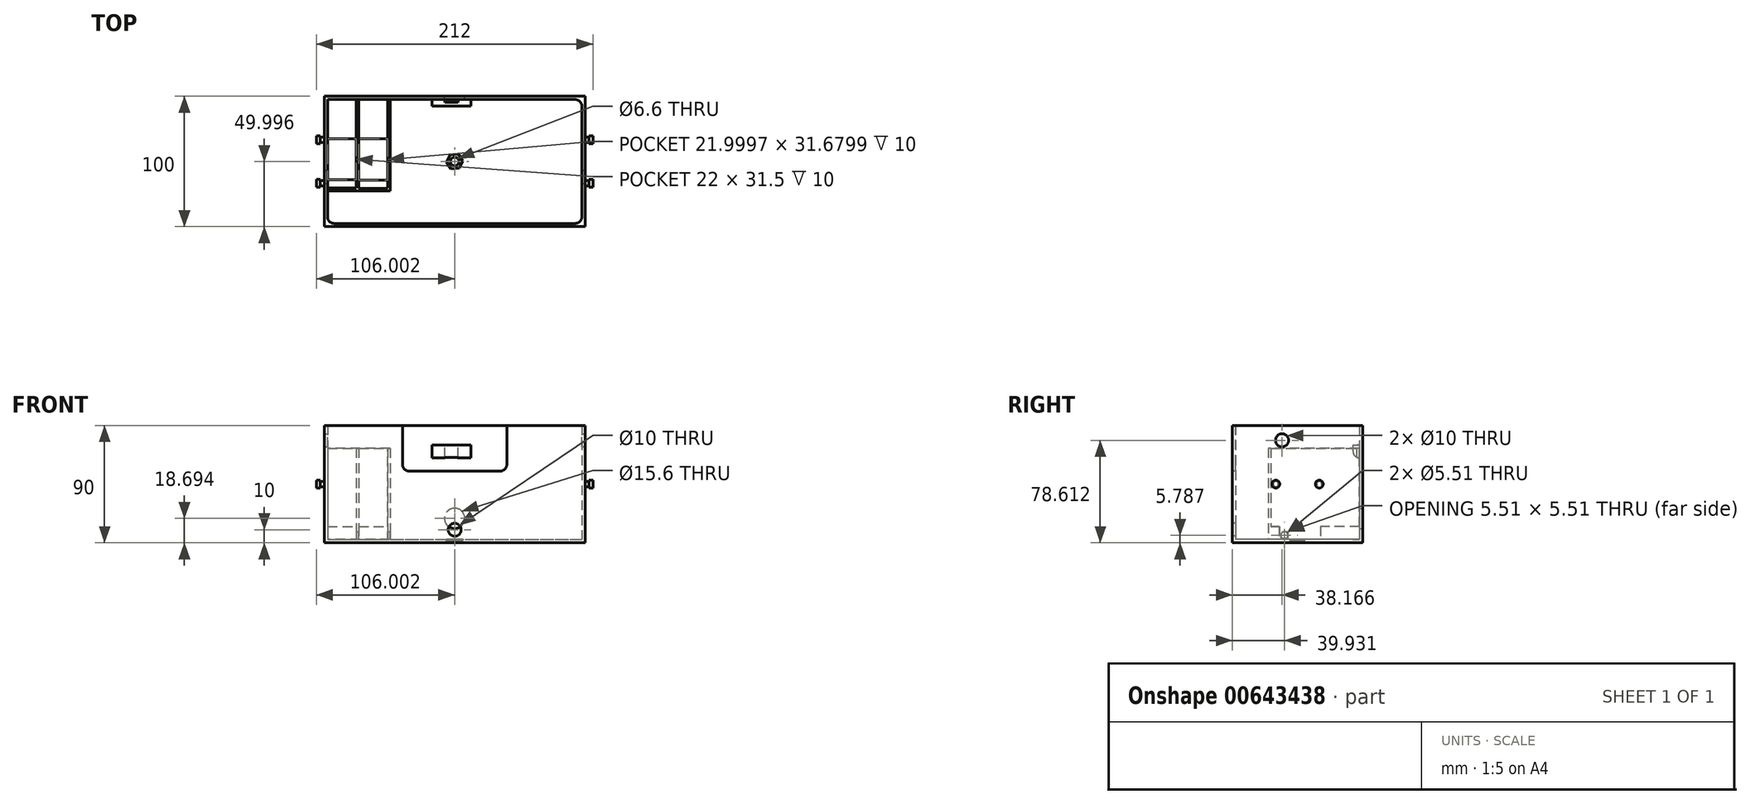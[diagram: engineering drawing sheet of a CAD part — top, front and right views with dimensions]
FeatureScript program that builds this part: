
annotation { "Feature Type Name" : "Feature", "Feature Type Description" : "" }
export const myFeature = defineFeature(function(context is Context, id is Id, definition is map)
    precondition{}
    {
        {
            var Q0;
            Q0=qCreatedBy(makeId("Top.planeOp"),FACE);
            var sketch = newSketch(context, id + "F0", { "sketchPlane" : qUnion([Q0])});
            skLineSegment(sketch, "E0.bottom", {"start": v(-106.92, 32.06) * mm, "end": v(93.08, 32.06) * mm});
            skLineSegment(sketch, "E0.top", {"start": v(-106.92, -67.94) * mm, "end": v(93.08, -67.94) * mm});
            skLineSegment(sketch, "E0.left", {"start": v(-106.92, 32.06) * mm, "end": v(-106.92, -67.94) * mm});
            skLineSegment(sketch, "E0.right", {"start": v(93.08, 32.06) * mm, "end": v(93.08, -67.94) * mm});
            skSolve(sketch);
        }
        {
            var Q0;
            Q0=makeQuery(id+"F0.imprint","IMPRINT",FACE,{"disambiguationData":[TD([[makeQuery(id+"F0.imprint","IMPRINT",EDGE,{"derivedFrom":sQuery(id+"F0.wireOp",EDGE,"E0.bottom")}),-1.0]])]});
            var Q1;
            Q1 = qSketchRegion(id + "FvAQ6DcHnj1znLy_1", true);
            extrude(context, id + "F1", {"entities" : qUnion([Q0, Q1]), "depth" : 90 * mm, "offsetDistance" : 25 * mm});
        }
        {
            var Q0;
            Q0=makeQuery(id+"F1.opExtrude","CAP_FACE",FACE,{"disambiguationData":[OSD([sQuery(id+"F0.wireOp",EDGE,"E0.bottom"),sQuery(id+"F0.wireOp",EDGE,"E0.top"),sQuery(id+"F0.wireOp",EDGE,"E0.left"),sQuery(id+"F0.wireOp",EDGE,"E0.right")])],"isStart":false});
            shell(context, id + "F2", {"entities" : qUnion([Q0]), "thickness" : 2.5 * mm});
        }
        {
            var Q0;
            Q0=makeQuery(id+"F2.opShell","OFFSET_FACE",FACE,{"disambiguationData":[OSD([sQuery(id+"F0.wireOp",EDGE,"E0.bottom"),sQuery(id+"F0.wireOp",EDGE,"E0.top"),sQuery(id+"F0.wireOp",EDGE,"E0.left"),sQuery(id+"F0.wireOp",EDGE,"E0.right")])]});
            var sketch = newSketch(context, id + "F3", { "sketchPlane" : qUnion([Q0])});
            skLineSegment(sketch, "E1", {"start": v(-104.42, 29.56) * mm, "end": v(-104.42, -38.44) * mm});
            skLineSegment(sketch, "E2", {"start": v(-104.42, -38.44) * mm, "end": v(-82.42, -38.44) * mm});
            skLineSegment(sketch, "E3", {"start": v(-82.42, -38.44) * mm, "end": v(-82.42, 29.56) * mm});
            skLineSegment(sketch, "E4", {"start": v(-82.42, 29.56) * mm, "end": v(-104.42, 29.56) * mm});
            skLineSegment(sketch, "E5", {"start": v(-82.42, 29.56) * mm, "end": v(-80.42, 29.56) * mm});
            skLineSegment(sketch, "E6", {"start": v(-80.42, 29.56) * mm, "end": v(-80.42, -38.62) * mm});
            skLineSegment(sketch, "E7", {"start": v(-80.42, -38.62) * mm, "end": v(-80.42, -40.44) * mm});
            skLineSegment(sketch, "E8", {"start": v(-80.42, -40.44) * mm, "end": v(-82.42, -40.44) * mm});
            skLineSegment(sketch, "E9", {"start": v(-82.42, -40.44) * mm, "end": v(-104.42, -40.44) * mm});
            skLineSegment(sketch, "E10", {"start": v(-104.42, -40.44) * mm, "end": v(-104.42, -38.44) * mm});
            skLineSegment(sketch, "E11", {"start": v(-80.42, 29.56) * mm, "end": v(-58.42, 29.56) * mm});
            skLineSegment(sketch, "E12", {"start": v(-58.42, 29.56) * mm, "end": v(-56.42, 29.56) * mm});
            skLineSegment(sketch, "E13", {"start": v(-56.42, 29.56) * mm, "end": v(-56.42, -38.44) * mm});
            skLineSegment(sketch, "E14", {"start": v(-56.42, -38.44) * mm, "end": v(-56.42, -40.44) * mm});
            skLineSegment(sketch, "E15", {"start": v(-56.42, -40.44) * mm, "end": v(-80.42, -40.44) * mm});
            skLineSegment(sketch, "E16", {"start": v(-80.42, -38.62) * mm, "end": v(-58.42, -38.44) * mm});
            skLineSegment(sketch, "E17", {"start": v(-58.42, -38.44) * mm, "end": v(-58.42, 29.56) * mm});
            skSolve(sketch);
        }
        {
            var Q0;
            Q0=makeQuery(id+"F3.imprint","IMPRINT",FACE,{"disambiguationData":[TD([[makeQuery(id+"F3.imprint","IMPRINT",EDGE,{"derivedFrom":sQuery(id+"F3.wireOp",EDGE,"E2")}),-1.0]])]});
            var Q1;
            Q1=makeQuery(id+"F3.imprint","IMPRINT",FACE,{"disambiguationData":[TD([[makeQuery(id+"F3.imprint","IMPRINT",EDGE,{"derivedFrom":sQuery(id+"F3.wireOp",EDGE,"E7")}),1.0]])]});
            extrude(context, id + "F4", {"entities" : qUnion([Q0, Q1]), "operationType" : NewBodyOperationType.ADD, "depth" : 70 * mm, "offsetDistance" : 25 * mm});
        }
        {
            var Q0;
            Q0=makeQuery(id+"F1.opExtrude","SWEPT_FACE",FACE,{"disambiguationData":[OSD([sQuery(id+"F0.wireOp",EDGE,"E0.top")])]});
            var sketch = newSketch(context, id + "F5", { "sketchPlane" : qUnion([Q0])});
            skLineSegment(sketch, "E18", {"start": v(-106.92, 90) * mm, "end": v(-46.92, 90) * mm, "construction": true});
            skLineSegment(sketch, "E19", {"start": v(-46.92, 90) * mm, "end": v(-46.92, 55) * mm});
            skLineSegment(sketch, "E20", {"start": v(-46.92, 55) * mm, "end": v(33.08, 55) * mm});
            skLineSegment(sketch, "E21", {"start": v(33.08, 55) * mm, "end": v(33.08, 90) * mm});
            skLineSegment(sketch, "E22", {"start": v(33.08, 90) * mm, "end": v(93.08, 90) * mm, "construction": true});
            skLineSegment(sketch, "E23", {"start": v(-6.92, 55) * mm, "end": v(-6.92, 10) * mm, "construction": true});
            skCircle(sketch, "E24", {"center": v(-6.92, 10) * mm, "radius": 5 * mm});
            skSolve(sketch);
        }
        {
            var Q0;
            {var subQ0=sQuery(id+"F5.wireOp",EDGE,"E19");Q0=makeQuery(id+"F5.imprint","IMPRINT",FACE,{"disambiguationData":[TD([[makeQuery(id+"F5.imprint","IMPRINT",EDGE,{"derivedFrom":subQ0}),1.0]])]});}
            var Q1;
            Q1=makeQuery(id+"F5.imprint","IMPRINT",FACE,{"disambiguationData":[TD([[makeQuery(id+"F5.imprint","IMPRINT",EDGE,{"derivedFrom":sQuery(id+"F5.wireOp",EDGE,"E24")}),1.0]])]});
            extrude(context, id + "F6", {"entities" : qUnion([Q0, Q1]), "operationType" : NewBodyOperationType.REMOVE, "oppositeDirection" : true, "depth" : 3 * mm, "offsetDistance" : 25 * mm});
        }
        {
            var Q0;
            Q0=makeQuery(id+"F1.opExtrude","CAP_FACE",FACE,{"disambiguationData":[OSD([sQuery(id+"F0.wireOp",EDGE,"E0.bottom"),sQuery(id+"F0.wireOp",EDGE,"E0.top"),sQuery(id+"F0.wireOp",EDGE,"E0.left"),sQuery(id+"F0.wireOp",EDGE,"E0.right")])],"isStart":true});
            var sketch = newSketch(context, id + "F7", { "sketchPlane" : qUnion([Q0])});
            skLineSegment(sketch, "E25", {"start": v(-6.92, 67.94) * mm, "end": v(-6.92, -32.06) * mm});
            skLineSegment(sketch, "E26", {"start": v(-106.92, 17.94) * mm, "end": v(93.08, 17.94) * mm, "construction": true});
            skCircle(sketch, "E27", {"center": v(-6.92, 17.94) * mm, "radius": 5.55 * mm, "construction": true});
            skLineSegment(sketch, "E28", {"start": v(-12.47, 14.74) * mm, "end": v(-12.47, 21.15) * mm});
            skLineSegment(sketch, "E29", {"start": v(-12.47, 21.15) * mm, "end": v(-6.92, 24.35) * mm});
            skLineSegment(sketch, "E30", {"start": v(-6.92, 24.35) * mm, "end": v(-1.37, 21.15) * mm});
            skLineSegment(sketch, "E31", {"start": v(-1.37, 21.15) * mm, "end": v(-1.37, 14.74) * mm});
            skLineSegment(sketch, "E32", {"start": v(-1.37, 14.74) * mm, "end": v(-6.92, 11.54) * mm});
            skLineSegment(sketch, "E33", {"start": v(-6.92, 11.54) * mm, "end": v(-12.47, 14.74) * mm});
            skCircle(sketch, "E34", {"center": v(-6.92, 17.94) * mm, "radius": 3.3 * mm});
            skSolve(sketch);
        }
        {
            var Q0;
            {var subQ0=sQuery(id+"F7.wireOp",EDGE,"E34");var subQ1=sQuery(id+"F7.wireOp",EDGE,"E25");var subQ2=makeQuery(id+"F7.imprint","INTERSECT",VERTEX,{"disambiguationData":[OD(0.0)],"derivedFrom":[subQ1,subQ0]});Q0=makeQuery(id+"F7.imprint","IMPRINT",FACE,{"disambiguationData":[TD([[makeQuery(id+"F7.imprint","IMPRINT",EDGE,{"disambiguationData":[TD([[subQ2,-1.0]])],"derivedFrom":subQ1}),1.0]])]});}
            var Q1;
            {var subQ0=sQuery(id+"F7.wireOp",EDGE,"E34");var subQ1=sQuery(id+"F7.wireOp",EDGE,"E25");var subQ2=makeQuery(id+"F7.imprint","INTERSECT",VERTEX,{"disambiguationData":[OD(0.0)],"derivedFrom":[subQ1,subQ0]});Q1=makeQuery(id+"F7.imprint","IMPRINT",FACE,{"disambiguationData":[TD([[makeQuery(id+"F7.imprint","IMPRINT",EDGE,{"disambiguationData":[TD([[subQ2,-1.0]])],"derivedFrom":subQ1}),-1.0]])]});}
            extrude(context, id + "F8", {"entities" : qUnion([Q0, Q1]), "operationType" : NewBodyOperationType.REMOVE, "oppositeDirection" : true, "depth" : 3 * mm, "offsetDistance" : 25 * mm});
        }
        {
            var Q0;
            {var subQ0=sQuery(id+"F0.wireOp",EDGE,"E0.right");var subQ1=sQuery(id+"F0.wireOp",EDGE,"E0.left");var subQ2=sQuery(id+"F0.wireOp",EDGE,"E0.top");var subQ3=sQuery(id+"F0.wireOp",EDGE,"E0.bottom");Q0=makeQuery(id+"F4.boolean.opBoolean","SPLIT",FACE,{"disambiguationData":[TD([makeQuery(id+"F2.opShell","OFFSET_FACE",FACE,{"disambiguationData":[OSD([subQ2])]})])],"derivedFrom":makeQuery(id+"F2.opShell","OFFSET_FACE",FACE,{"disambiguationData":[OSD([subQ3,subQ2,subQ1,subQ0])]})});}
            var sketch = newSketch(context, id + "F9", { "sketchPlane" : qUnion([Q0])});
            skCircle(sketch, "E35.cCircle", {"center": v(-6.92, -17.94) * mm, "radius": 6.25 * mm, "construction": true});
            skLineSegment(sketch, "E35.0", {"start": v(-10.37, -12.74) * mm, "end": v(-4.13, -12.35) * mm});
            skLineSegment(sketch, "E35.1", {"start": v(-4.13, -12.35) * mm, "end": v(-0.68, -17.56) * mm});
            skLineSegment(sketch, "E35.2", {"start": v(-0.68, -17.56) * mm, "end": v(-3.46, -23.15) * mm});
            skLineSegment(sketch, "E35.3", {"start": v(-3.46, -23.15) * mm, "end": v(-9.7, -23.54) * mm});
            skLineSegment(sketch, "E35.4", {"start": v(-9.7, -23.54) * mm, "end": v(-13.16, -18.33) * mm});
            skLineSegment(sketch, "E35.5", {"start": v(-13.16, -18.33) * mm, "end": v(-10.37, -12.74) * mm});
            skSolve(sketch);
        }
        {
            var Q0;
            Q0=makeQuery(id+"F9.imprint","IMPRINT",FACE,{"disambiguationData":[TD([[makeQuery(id+"F9.imprint","IMPRINT",EDGE,{"derivedFrom":sQuery(id+"F9.wireOp",EDGE,"E35.0")}),-1.0]])]});
            extrude(context, id + "F10", {"entities" : qUnion([Q0]), "operationType" : NewBodyOperationType.REMOVE, "oppositeDirection" : true, "depth" : 1.5 * mm, "offsetDistance" : 25 * mm});
        }
        {
            var Q0;
            Q0=makeQuery(id+"F1.opExtrude","SWEPT_FACE",FACE,{"disambiguationData":[OSD([sQuery(id+"F0.wireOp",EDGE,"E0.bottom")])]});
            var sketch = newSketch(context, id + "F11", { "sketchPlane" : qUnion([Q0])});
            skCircle(sketch, "E36", {"center": v(6.92, 18.7) * mm, "radius": 7.8 * mm});
            skPoint(sketch, "E36.centerSnap0", {"position": v(6.92, 0) * mm});
            skSolve(sketch);
        }
        {
            var Q0;
            Q0=makeQuery(id+"F11.imprint","IMPRINT",FACE,{"disambiguationData":[TD([[makeQuery(id+"F11.imprint","IMPRINT",EDGE,{"derivedFrom":sQuery(id+"F11.wireOp",EDGE,"E36")}),1.0]])]});
            extrude(context, id + "F12", {"entities" : qUnion([Q0]), "operationType" : NewBodyOperationType.REMOVE, "oppositeDirection" : true, "depth" : 3 * mm, "offsetDistance" : 25 * mm});
        }
        {
            var Q0;
            Q0=makeQuery(id+"F2.opShell","OFFSET_EDGE",EDGE,{"disambiguationData":[OSD([sQuery(id+"F0.wireOp",EDGE,"E0.bottom"),sQuery(id+"F0.wireOp",EDGE,"E0.right")])]});
            var Q1;
            Q1=makeQuery(id+"F2.opShell","OFFSET_EDGE",EDGE,{"disambiguationData":[OSD([sQuery(id+"F0.wireOp",EDGE,"E0.top"),sQuery(id+"F0.wireOp",EDGE,"E0.right")])]});
            var Q2;
            Q2=makeQuery(id+"F2.opShell","OFFSET_EDGE",EDGE,{"disambiguationData":[OSD([sQuery(id+"F0.wireOp",EDGE,"E0.top"),sQuery(id+"F0.wireOp",EDGE,"E0.left")])]});
            fillet(context, id + "F13", {"entities" : qUnion([Q0, Q1, Q2]), "radius" : 5 * mm, "tangentPropagation" : true, "allowEdgeOverflow" : false});
        }
        {
            var Q0;
            Q0=makeQuery(id+"F6.boolean.opBoolean","COPY",EDGE,{"derivedFrom":makeQuery(id+"F6.opExtrude","SWEPT_EDGE",EDGE,{"disambiguationData":[OSD([sQuery(id+"F5.wireOp",EDGE,"E20"),sQuery(id+"F5.wireOp",EDGE,"E21")])]})});
            var Q1;
            Q1=makeQuery(id+"F6.boolean.opBoolean","COPY",EDGE,{"derivedFrom":makeQuery(id+"F6.opExtrude","SWEPT_EDGE",EDGE,{"disambiguationData":[OSD([sQuery(id+"F5.wireOp",EDGE,"E19"),sQuery(id+"F5.wireOp",EDGE,"E20")])]})});
            var Q2;
            Q2=makeQuery(id+"F6.boolean.opBoolean","COPY",EDGE,{"derivedFrom":makeQuery(id+"F6.opExtrude","SWEPT_EDGE",EDGE,{"disambiguationData":[OSD([sQuery(id+"F0.wireOp",EDGE,"E0.top"),sQuery(id+"F5.wireOp",EDGE,"E19")])]})});
            var Q3;
            Q3=makeQuery(id+"F6.boolean.opBoolean","COPY",EDGE,{"derivedFrom":makeQuery(id+"F6.opExtrude","SWEPT_EDGE",EDGE,{"disambiguationData":[OSD([sQuery(id+"F0.wireOp",EDGE,"E0.top"),sQuery(id+"F5.wireOp",EDGE,"E21")])]})});
            fillet(context, id + "F14", {"entities" : qUnion([Q0, Q1, Q2, Q3]), "radius" : 5 * mm, "tangentPropagation" : true, "allowEdgeOverflow" : false});
        }
        {
            var Q0;
            Q0=makeQuery(id+"F1.opExtrude","SWEPT_FACE",FACE,{"disambiguationData":[OSD([sQuery(id+"F0.wireOp",EDGE,"E0.right")])]});
            var sketch = newSketch(context, id + "F15", { "sketchPlane" : qUnion([Q0])});
            skLineSegment(sketch, "E37", {"start": v(-67.94, 45) * mm, "end": v(-34.61, 45) * mm});
            skLineSegment(sketch, "E38", {"start": v(-34.61, 45) * mm, "end": v(-1.28, 45) * mm});
            skLineSegment(sketch, "E39", {"start": v(-1.28, 45) * mm, "end": v(32.06, 45) * mm});
            skCircle(sketch, "E40", {"center": v(-34.61, 45) * mm, "radius": 2 * mm});
            skCircle(sketch, "E41", {"center": v(-1.28, 45) * mm, "radius": 2 * mm});
            skSolve(sketch);
        }
        {
            var Q0;
            Q0 = qSketchRegion(id + "F15", true);
            extrude(context, id + "F16", {"entities" : qUnion([Q0]), "operationType" : NewBodyOperationType.ADD, "depth" : 3 * mm, "offsetDistance" : 25 * mm});
        }
        {
            var Q0;
            Q0=makeQuery(id+"F16.opExtrude","CAP_FACE",FACE,{"disambiguationData":[OSD([sQuery(id+"F15.wireOp",EDGE,"E40")])],"isStart":false});
            var sketch = newSketch(context, id + "F17", { "sketchPlane" : qUnion([Q0])});
            skCircle(sketch, "E42", {"center": v(-1.28, 45) * mm, "radius": 3 * mm});
            skSolve(sketch);
        }
        {
            var Q0;
            Q0=makeQuery(id+"F17.imprint","IMPRINT",FACE,{"disambiguationData":[TD([[makeQuery(id+"F17.imprint","IMPRINT",EDGE,{"derivedFrom":makeQuery(id+"F16.opExtrude","CAP_EDGE",EDGE,{"disambiguationData":[OSD([sQuery(id+"F15.wireOp",EDGE,"E40")])],"isStart":false})}),1.0]])]});
            var sketch = newSketch(context, id + "F18", { "sketchPlane" : qUnion([Q0])});
            skCircle(sketch, "E43", {"center": v(-34.61, 45) * mm, "radius": 3 * mm});
            skSolve(sketch);
        }
        {
            var Q0;
            Q0=makeQuery(id+"F17.imprint","IMPRINT",FACE,{"disambiguationData":[TD([[makeQuery(id+"F17.imprint","IMPRINT",EDGE,{"derivedFrom":makeQuery(id+"F16.opExtrude","CAP_EDGE",EDGE,{"disambiguationData":[OSD([sQuery(id+"F15.wireOp",EDGE,"E40")])],"isStart":false})}),1.0]])]});
            var Q1;
            Q1=makeQuery(id+"F18.imprint","IMPRINT",FACE,{"disambiguationData":[TD([[makeQuery(id+"F18.imprint","IMPRINT",EDGE,{"derivedFrom":sQuery(id+"F18.wireOp",EDGE,"E43")}),1.0]])]});
            var Q2;
            Q2=makeQuery(id+"F17.imprint","IMPRINT",FACE,{"disambiguationData":[TD([[makeQuery(id+"F17.imprint","IMPRINT",EDGE,{"derivedFrom":sQuery(id+"F17.wireOp",EDGE,"E42")}),1.0]])]});
            extrude(context, id + "F19", {"entities" : qUnion([Q0, Q1, Q2]), "operationType" : NewBodyOperationType.ADD, "depth" : 3 * mm, "offsetDistance" : 25 * mm});
        }
        {
            var Q0;
            Q0=makeQuery(id+"F1.opExtrude","SWEPT_FACE",FACE,{"disambiguationData":[OSD([sQuery(id+"F0.wireOp",EDGE,"E0.left")])]});
            var sketch = newSketch(context, id + "F20", { "sketchPlane" : qUnion([Q0])});
            skLineSegment(sketch, "E44", {"start": v(-32.06, 45) * mm, "end": v(1.28, 45) * mm});
            skLineSegment(sketch, "E45", {"start": v(1.28, 45) * mm, "end": v(34.61, 45) * mm});
            skLineSegment(sketch, "E46", {"start": v(34.61, 45) * mm, "end": v(67.94, 45) * mm});
            skCircle(sketch, "E47", {"center": v(1.28, 45) * mm, "radius": 2 * mm});
            skCircle(sketch, "E48", {"center": v(34.61, 45) * mm, "radius": 2 * mm});
            skSolve(sketch);
        }
        {
            var Q0;
            {var subQ0=sQuery(id+"F20.wireOp",EDGE,"E45");var subQ1=sQuery(id+"F20.wireOp",EDGE,"E44");var subQ2=makeQuery(id+"F20.imprint","INTERSECT",VERTEX,{"derivedFrom":[subQ1,subQ0]});Q0=makeQuery(id+"F20.imprint","IMPRINT",FACE,{"disambiguationData":[TD([[makeQuery(id+"F20.imprint","IMPRINT",EDGE,{"disambiguationData":[TD([[subQ2,1.0]])],"derivedFrom":subQ1}),1.0]])]});}
            var Q1;
            {var subQ0=sQuery(id+"F20.wireOp",EDGE,"E45");var subQ1=sQuery(id+"F20.wireOp",EDGE,"E44");var subQ2=makeQuery(id+"F20.imprint","INTERSECT",VERTEX,{"derivedFrom":[subQ1,subQ0]});Q1=makeQuery(id+"F20.imprint","IMPRINT",FACE,{"disambiguationData":[TD([[makeQuery(id+"F20.imprint","IMPRINT",EDGE,{"disambiguationData":[TD([[subQ2,1.0]])],"derivedFrom":subQ1}),-1.0]])]});}
            var Q2;
            {var subQ0=sQuery(id+"F20.wireOp",EDGE,"E46");var subQ1=sQuery(id+"F20.wireOp",EDGE,"E45");var subQ2=makeQuery(id+"F20.imprint","INTERSECT",VERTEX,{"derivedFrom":[subQ1,subQ0]});Q2=makeQuery(id+"F20.imprint","IMPRINT",FACE,{"disambiguationData":[TD([[makeQuery(id+"F20.imprint","IMPRINT",EDGE,{"disambiguationData":[TD([[subQ2,1.0]])],"derivedFrom":subQ1}),1.0]])]});}
            var Q3;
            {var subQ0=sQuery(id+"F20.wireOp",EDGE,"E46");var subQ1=sQuery(id+"F20.wireOp",EDGE,"E45");var subQ2=makeQuery(id+"F20.imprint","INTERSECT",VERTEX,{"derivedFrom":[subQ1,subQ0]});Q3=makeQuery(id+"F20.imprint","IMPRINT",FACE,{"disambiguationData":[TD([[makeQuery(id+"F20.imprint","IMPRINT",EDGE,{"disambiguationData":[TD([[subQ2,1.0]])],"derivedFrom":subQ1}),-1.0]])]});}
            extrude(context, id + "F21", {"entities" : qUnion([Q0, Q1, Q2, Q3]), "operationType" : NewBodyOperationType.ADD, "depth" : 3 * mm, "offsetDistance" : 25 * mm});
        }
        {
            var Q0;
            Q0=makeQuery(id+"F21.opExtrude","CAP_FACE",FACE,{"disambiguationData":[OSD([sQuery(id+"F20.wireOp",EDGE,"E47")])],"isStart":false});
            var sketch = newSketch(context, id + "F22", { "sketchPlane" : qUnion([Q0])});
            skCircle(sketch, "E49", {"center": v(1.28, 45) * mm, "radius": 3 * mm});
            skCircle(sketch, "E50", {"center": v(34.61, 45) * mm, "radius": 3 * mm});
            skSolve(sketch);
        }
        {
            var Q0;
            Q0=makeQuery(id+"F22.imprint","IMPRINT",FACE,{"disambiguationData":[TD([[makeQuery(id+"F22.imprint","IMPRINT",EDGE,{"derivedFrom":sQuery(id+"F22.wireOp",EDGE,"E49")}),1.0]])]});
            var Q1;
            Q1=makeQuery(id+"F22.imprint","IMPRINT",FACE,{"disambiguationData":[TD([[makeQuery(id+"F22.imprint","IMPRINT",EDGE,{"derivedFrom":makeQuery(id+"F21.opExtrude","CAP_EDGE",EDGE,{"disambiguationData":[OSD([sQuery(id+"F20.wireOp",EDGE,"E47")])],"isStart":false})}),1.0]])]});
            var Q2;
            Q2=makeQuery(id+"F22.imprint","IMPRINT",FACE,{"disambiguationData":[TD([[makeQuery(id+"F22.imprint","IMPRINT",EDGE,{"derivedFrom":sQuery(id+"F22.wireOp",EDGE,"E50")}),1.0]])]});
            extrude(context, id + "F23", {"entities" : qUnion([Q0, Q1, Q2]), "operationType" : NewBodyOperationType.ADD, "depth" : 3 * mm, "offsetDistance" : 25 * mm});
        }
        {
            var Q0;
            Q0=makeQuery(id+"F2.opShell","OFFSET_FACE",FACE,{"disambiguationData":[OSD([sQuery(id+"F0.wireOp",EDGE,"E0.left")])]});
            var sketch = newSketch(context, id + "F24", { "sketchPlane" : qUnion([Q0])});
            skCircle(sketch, "E51", {"center": v(-29.77, 78.61) * mm, "radius": 5 * mm});
            skSolve(sketch);
        }
        {
            var Q0;
            Q0=makeQuery(id+"F24.imprint","IMPRINT",FACE,{"disambiguationData":[TD([[makeQuery(id+"F24.imprint","IMPRINT",EDGE,{"derivedFrom":sQuery(id+"F24.wireOp",EDGE,"E51")}),1.0]])]});
            extrude(context, id + "F25", {"entities" : qUnion([Q0]), "operationType" : NewBodyOperationType.REMOVE, "endBound" : BoundingType.SYMMETRIC, "oppositeDirection" : true, "depth" : 800 * mm, "offsetDistance" : 25 * mm});
        }
        {
            var Q0;
            {var subQ0=sQuery(id+"F0.wireOp",EDGE,"E0.bottom");var subQ1=sQuery(id+"F0.wireOp",EDGE,"E0.left");Q0=makeQuery(id+"F4.boolean.opBoolean","SPLIT",FACE,{"disambiguationData":[TD([makeQuery(id+"F4.opExtrude","SWEPT_FACE",FACE,{"disambiguationData":[OSD([sQuery(id+"F3.wireOp",EDGE,"E2")])]})])],"derivedFrom":makeQuery(id+"F2.opShell","OFFSET_FACE",FACE,{"disambiguationData":[OSD([subQ0,sQuery(id+"F0.wireOp",EDGE,"E0.top"),subQ1,sQuery(id+"F0.wireOp",EDGE,"E0.right")])]})});}
            var sketch = newSketch(context, id + "F26", { "sketchPlane" : qUnion([Q0])});
            skLineSegment(sketch, "E52.bottom", {"start": v(-104.42, 29.56) * mm, "end": v(-82.42, 29.56) * mm});
            skLineSegment(sketch, "E52.top", {"start": v(-104.42, -0.44) * mm, "end": v(-82.42, -0.44) * mm});
            skLineSegment(sketch, "E52.left", {"start": v(-104.42, 29.56) * mm, "end": v(-104.42, -0.44) * mm});
            skLineSegment(sketch, "E52.right", {"start": v(-82.42, 29.56) * mm, "end": v(-82.42, -0.44) * mm});
            skLineSegment(sketch, "E53.bottom", {"start": v(-104.42, -38.44) * mm, "end": v(-82.42, -38.44) * mm});
            skLineSegment(sketch, "E53.top", {"start": v(-104.42, -31.94) * mm, "end": v(-82.42, -31.94) * mm});
            skLineSegment(sketch, "E53.left", {"start": v(-104.42, -38.44) * mm, "end": v(-104.42, -31.94) * mm});
            skLineSegment(sketch, "E53.right", {"start": v(-82.42, -38.44) * mm, "end": v(-82.42, -31.94) * mm});
            skSolve(sketch);
        }
        {
            var Q0;
            {var subQ0=sQuery(id+"F0.wireOp",EDGE,"E0.bottom");Q0=makeQuery(id+"F4.boolean.opBoolean","SPLIT",FACE,{"disambiguationData":[TD([makeQuery(id+"F4.opExtrude","SWEPT_FACE",FACE,{"disambiguationData":[OSD([sQuery(id+"F3.wireOp",EDGE,"E6")])]})])],"derivedFrom":makeQuery(id+"F2.opShell","OFFSET_FACE",FACE,{"disambiguationData":[OSD([subQ0,sQuery(id+"F0.wireOp",EDGE,"E0.top"),sQuery(id+"F0.wireOp",EDGE,"E0.left"),sQuery(id+"F0.wireOp",EDGE,"E0.right")])]})});}
            var sketch = newSketch(context, id + "F27", { "sketchPlane" : qUnion([Q0])});
            skLineSegment(sketch, "E54.bottom", {"start": v(-80.42, 29.56) * mm, "end": v(-58.42, 29.56) * mm});
            skLineSegment(sketch, "E54.top", {"start": v(-80.42, -0.44) * mm, "end": v(-58.42, -0.44) * mm});
            skLineSegment(sketch, "E54.left", {"start": v(-80.42, 29.56) * mm, "end": v(-80.42, -0.44) * mm});
            skLineSegment(sketch, "E54.right", {"start": v(-58.42, 29.56) * mm, "end": v(-58.42, -0.44) * mm});
            skSolve(sketch);
        }
        {
            var Q0;
            {var subQ0=sQuery(id+"F0.wireOp",EDGE,"E0.bottom");Q0=makeQuery(id+"F4.boolean.opBoolean","SPLIT",FACE,{"disambiguationData":[TD([makeQuery(id+"F4.opExtrude","SWEPT_FACE",FACE,{"disambiguationData":[OSD([sQuery(id+"F3.wireOp",EDGE,"E6")])]})])],"derivedFrom":makeQuery(id+"F2.opShell","OFFSET_FACE",FACE,{"disambiguationData":[OSD([subQ0,sQuery(id+"F0.wireOp",EDGE,"E0.top"),sQuery(id+"F0.wireOp",EDGE,"E0.left"),sQuery(id+"F0.wireOp",EDGE,"E0.right")])]})});}
            var sketch = newSketch(context, id + "F28", { "sketchPlane" : qUnion([Q0])});
            skLineSegment(sketch, "E55.bottom", {"start": v(-80.42, -38.62) * mm, "end": v(-58.42, -38.62) * mm});
            skLineSegment(sketch, "E55.top", {"start": v(-80.42, -32.12) * mm, "end": v(-58.42, -32.12) * mm});
            skLineSegment(sketch, "E55.left", {"start": v(-80.42, -38.62) * mm, "end": v(-80.42, -32.12) * mm});
            skLineSegment(sketch, "E55.right", {"start": v(-58.42, -38.62) * mm, "end": v(-58.42, -32.12) * mm});
            skSolve(sketch);
        }
        {
            var Q0;
            Q0=makeQuery(id+"F26.imprint","IMPRINT",FACE,{"disambiguationData":[TD([[makeQuery(id+"F26.imprint","IMPRINT",EDGE,{"derivedFrom":sQuery(id+"F26.wireOp",EDGE,"E52.bottom")}),-1.0]])]});
            var Q1;
            Q1=makeQuery(id+"F27.imprint","IMPRINT",FACE,{"disambiguationData":[TD([[makeQuery(id+"F27.imprint","IMPRINT",EDGE,{"derivedFrom":sQuery(id+"F27.wireOp",EDGE,"E54.bottom")}),-1.0]])]});
            var Q2;
            {var subQ0=sQuery(id+"F28.wireOp",EDGE,"E55.top");Q2=makeQuery(id+"F28.imprint","IMPRINT",FACE,{"disambiguationData":[TD([[makeQuery(id+"F28.imprint","IMPRINT",EDGE,{"derivedFrom":subQ0}),-1.0]])]});}
            var Q3;
            Q3=makeQuery(id+"F26.imprint","IMPRINT",FACE,{"disambiguationData":[TD([[makeQuery(id+"F26.imprint","IMPRINT",EDGE,{"derivedFrom":sQuery(id+"F26.wireOp",EDGE,"E53.bottom")}),1.0]])]});
            extrude(context, id + "F29", {"entities" : qUnion([Q0, Q1, Q2, Q3]), "operationType" : NewBodyOperationType.ADD, "depth" : 10 * mm, "offsetDistance" : 25 * mm});
        }
        {
            var Q0;
            Q0=makeQuery(id+"F4.opExtrude","SWEPT_FACE",FACE,{"disambiguationData":[OSD([sQuery(id+"F3.wireOp",EDGE,"E13"),sQuery(id+"F3.wireOp",EDGE,"E14")])]});
            var sketch = newSketch(context, id + "F30", { "sketchPlane" : qUnion([Q0])});
            skLineSegment(sketch, "E56", {"start": v(-40.44, 2.5) * mm, "end": v(-40.44, 4.5) * mm});
            skLineSegment(sketch, "E57", {"start": v(-40.44, 4.5) * mm, "end": v(-30.44, 4.5) * mm});
            skCircle(sketch, "E58", {"center": v(-28, 5.79) * mm, "radius": 2.75 * mm});
            skPoint(sketch, "E58.second.point", {"position": v(-25.38, 6.6) * mm});
            skPoint(sketch, "E58.third.point", {"position": v(-25.57, 4.5) * mm});
            skSolve(sketch);
        }
        {
            var Q0;
            Q0=makeQuery(id+"F2.opShell","OFFSET_FACE",FACE,{"disambiguationData":[OSD([sQuery(id+"F0.wireOp",EDGE,"E0.bottom")])]});
            var sketch = newSketch(context, id + "F31", { "sketchPlane" : qUnion([Q0])});
            skPoint(sketch, "E59.firstSnap0", {"position": v(-9.42, 90) * mm});
            skLineSegment(sketch, "E59.bottom", {"start": v(-9.42, 75.1) * mm, "end": v(5.58, 75.1) * mm});
            skLineSegment(sketch, "E59.top", {"start": v(-9.42, 65.1) * mm, "end": v(5.58, 65.1) * mm});
            skLineSegment(sketch, "E59.left", {"start": v(-9.42, 75.1) * mm, "end": v(-9.42, 65.1) * mm});
            skLineSegment(sketch, "E59.right", {"start": v(5.58, 75.1) * mm, "end": v(5.58, 65.1) * mm});
            skLineSegment(sketch, "E60.bottom", {"start": v(-9.42, 75.1) * mm, "end": v(-24.42, 75.1) * mm});
            skLineSegment(sketch, "E60.top", {"start": v(-9.42, 65.1) * mm, "end": v(-24.42, 65.1) * mm});
            skLineSegment(sketch, "E60.right", {"start": v(-24.42, 75.1) * mm, "end": v(-24.42, 65.1) * mm});
            skSolve(sketch);
        }
        {
            var Q0;
            Q0=makeQuery(id+"F31.imprint","IMPRINT",FACE,{"disambiguationData":[TD([[makeQuery(id+"F31.imprint","IMPRINT",EDGE,{"derivedFrom":sQuery(id+"F31.wireOp",EDGE,"E60.bottom")}),1.0]])]});
            var Q1;
            Q1=makeQuery(id+"F31.imprint","IMPRINT",FACE,{"disambiguationData":[TD([[makeQuery(id+"F31.imprint","IMPRINT",EDGE,{"derivedFrom":sQuery(id+"F31.wireOp",EDGE,"E59.bottom")}),-1.0]])]});
            extrude(context, id + "F32", {"entities" : qUnion([Q0, Q1]), "operationType" : NewBodyOperationType.ADD, "depth" : 5 * mm, "offsetDistance" : 25 * mm});
        }
        {
            var Q0;
            Q0=makeQuery(id+"F32.opExtrude","SWEPT_FACE",FACE,{"disambiguationData":[OSD([sQuery(id+"F31.wireOp",EDGE,"E59.bottom"),sQuery(id+"F31.wireOp",EDGE,"E60.bottom")])]});
            var sketch = newSketch(context, id + "F33", { "sketchPlane" : qUnion([Q0])});
            skLineSegment(sketch, "E61", {"start": v(-24.42, 29.56) * mm, "end": v(-14.42, 29.56) * mm, "construction": true});
            skLineSegment(sketch, "E62", {"start": v(-14.42, 29.56) * mm, "end": v(-4.42, 29.56) * mm});
            skLineSegment(sketch, "E63", {"start": v(-4.42, 29.56) * mm, "end": v(5.58, 29.56) * mm, "construction": true});
            skLineSegment(sketch, "E64", {"start": v(-14.42, 29.56) * mm, "end": v(-14.42, 27.56) * mm});
            skLineSegment(sketch, "E65", {"start": v(-14.42, 27.56) * mm, "end": v(-4.42, 27.56) * mm});
            skLineSegment(sketch, "E66", {"start": v(-4.42, 27.56) * mm, "end": v(-4.42, 29.56) * mm});
            skSolve(sketch);
        }
        {
            var Q0;
            Q0=makeQuery(id+"F33.imprint","IMPRINT",FACE,{"disambiguationData":[TD([[makeQuery(id+"F33.imprint","IMPRINT",EDGE,{"derivedFrom":sQuery(id+"F33.wireOp",EDGE,"E62")}),1.0]])]});
            extrude(context, id + "F34", {"entities" : qUnion([Q0]), "operationType" : NewBodyOperationType.REMOVE, "oppositeDirection" : true, "depth" : 10 * mm, "offsetDistance" : 25 * mm});
        }
        {
            var Q0;
            {var subQ0=sQuery(id+"F31.wireOp",EDGE,"E60.bottom");var subQ1=sQuery(id+"F31.wireOp",EDGE,"E59.bottom");Q0=makeQuery(id+"F34.boolean.opBoolean","SPLIT",EDGE,{"disambiguationData":[TD([makeQuery(id+"F32.opExtrude","SWEPT_FACE",FACE,{"disambiguationData":[OSD([sQuery(id+"F31.wireOp",EDGE,"E59.right")])]})])],"derivedFrom":makeQuery(id+"F32.opExtrude","CAP_EDGE",EDGE,{"disambiguationData":[OSD([subQ1,subQ0])],"isStart":true})});}
            var Q1;
            Q1=makeQuery(id+"F32.opExtrude","CAP_EDGE",EDGE,{"disambiguationData":[OSD([sQuery(id+"F31.wireOp",EDGE,"E59.top"),sQuery(id+"F31.wireOp",EDGE,"E60.top")])],"isStart":false});
            fillet(context, id + "F35", {"entities" : qUnion([Q0, Q1]), "radius" : 5 * mm, "tangentPropagation" : true, "allowEdgeOverflow" : false});
        }
        {
            var Q0;
            Q0 = qSketchRegion(id + "F30", true);
            extrude(context, id + "F36", {"entities" : qUnion([Q0]), "operationType" : NewBodyOperationType.REMOVE, "oppositeDirection" : true, "depth" : 35 * mm, "offsetDistance" : 25 * mm});
        }
    });
